# Revit family: PRD_AR_FlshCntrlDvcs_UrinalUnit_ACEF3002
name_source: partatom
category: Plumbing Fixtures
units: mm (PartAtom-declared; Revit-internal decimal feet)

## family parameters
Always vertical = Yes
Cut with Voids When Loaded = No
OmniClass Number = 23.65.55.14.17
OmniClass Title = Adjusting/Controlling Valves for Liquid Services
Part Type = Normal
Room Calculation Point = No
Round Connector Dimension = Use Diameter
Shared = No
Work Plane-Based = No

## types (1)
- ACEF3002
    AssetType = Fixed
    BIMObjectName = PRD_AR_FlushControlDevices_UrinalUnit_ACEF3002
    BodyMaterial = <By Category>
    Category = Pr_75_50_46_31, Flush control devices
    CloseOffRating = 0.0 Pa
    Default Elevation = 0 mm  [stored 0 ft]
    Description = F5 smart urinal unit for installation behind single urinals made of ceramic. Water path pre-assembled with inlet connector, hoses, locking and solenoid valve. Control unit in sealed plastic box for wireless communication with the F5 smart urinal sensor. Either for battery operation with 6 V lithium battery (CR-P2) per control unit or separate power supply via power supply unit 6.75 V/12 V DC.
Battery compartment including battery or power supply unit with extension cable must be ordered separately.
    DurationUnit = year
    Features = for installation behind single urinals made of ceramic
    FlowCoefficient = 0
    FlushingRate = 0.0 L/s
    HasIntegralShutOffDevice = No
    IfcExportAs = IfcValveType
    IfcExportType = FLUSHING
    IsHighPressure = No
    Manufacturer = KWC Group AG
    ManufacturerName = KWC Group AG
    ManufacturerURL = www.kwc.com
    Model = ACEF3002
    ModelNumber = 2030067532
    ModelReference = ACEF3002
    NBSDescription = Flush control devices
    NBSReference = 90-15-35/470
    Name = F5 smart urinal unit for single ceramic urinals ACEF3002
    NominalDepth = 0 mm  [stored 0 ft]
    NominalHeight = 0 mm  [stored 0 ft]
    NominalWidth = 0 mm  [stored 0 ft]
    PowerConsumption = 1.8 Voltampere
    PowerSupplyConnection = 6,75 / 12 V DC
    ProductInformation = http://pim.kwc.com
    ProtectiveSystemIP = IP 68
    Quantity = 1
    QuantityUom = piece
    Size = 0.000000000000
    Status = New
    TailorMade = no
    TestPressure = 0.0 Pa
    URL = www.kwc.com
    Uniclass2015Code = Pr_75_50_46_31
    Uniclass2015Title = Flush control devices
    Uniclass2015Version = Products v1.32
    ValveMechanism = OTHER
    ValveOperation = OTHER
    ValvePattern = OTHER
    Version = 1
    WarrantyDurationUnit = year
    WorkingPressure = 0.0 Pa

note: [stored X ft] marks values corroborated as IEEE doubles in the binary element streams (Revit-internal decimal feet)

## geometry (parser evidence)
native form markers: Sweep x6
no freeform markers — native parametric forms only
